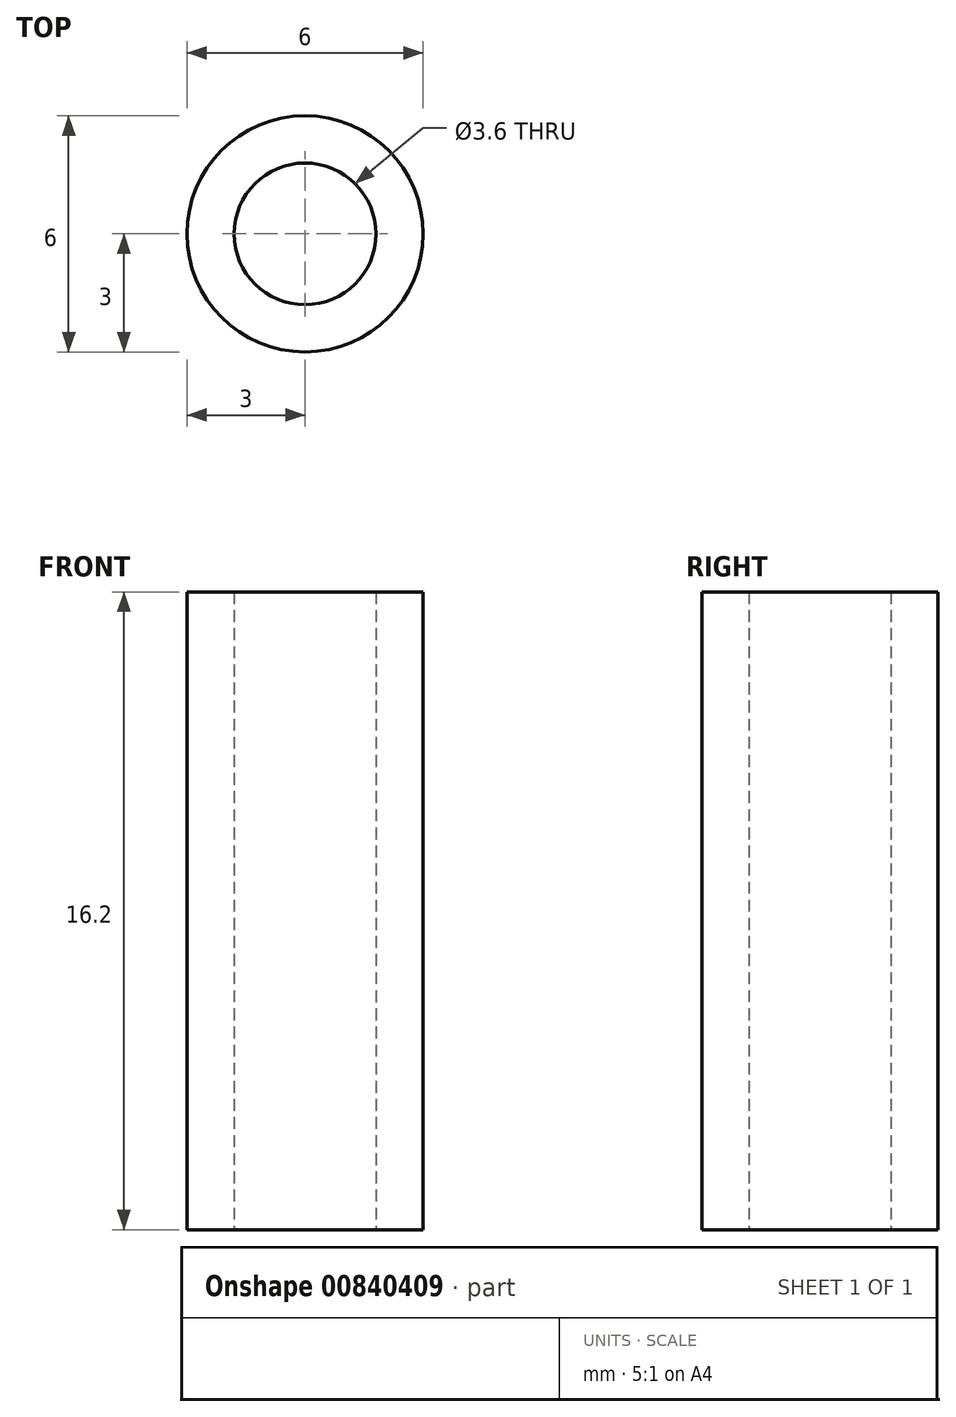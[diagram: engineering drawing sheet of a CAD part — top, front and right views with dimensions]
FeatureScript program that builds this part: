
annotation { "Feature Type Name" : "Feature", "Feature Type Description" : "" }
export const myFeature = defineFeature(function(context is Context, id is Id, definition is map)
    precondition{}
    {
        {
            var Q0;
            Q0=qCreatedBy(makeId("Top.planeOp"),FACE);
            var sketch = newSketch(context, id + "F0", { "sketchPlane" : qUnion([Q0])});
            skCircle(sketch, "E0", {"center": v(0, 0) * mm, "radius": 1.8 * mm});
            skCircle(sketch, "E1", {"center": v(0, 0) * mm, "radius": 3 * mm});
            skSolve(sketch);
        }
        {
            var Q0;
            Q0=makeQuery(id+"F0.imprint","IMPRINT",FACE,{"disambiguationData":[TD([[makeQuery(id+"F0.imprint","IMPRINT",EDGE,{"derivedFrom":sQuery(id+"F0.wireOp",EDGE,"E0")}),-1.0]])]});
            extrude(context, id + "F1", {"entities" : qUnion([Q0]), "depth" : 16.2 * mm, "offsetDistance" : 25 * mm});
        }
    });
